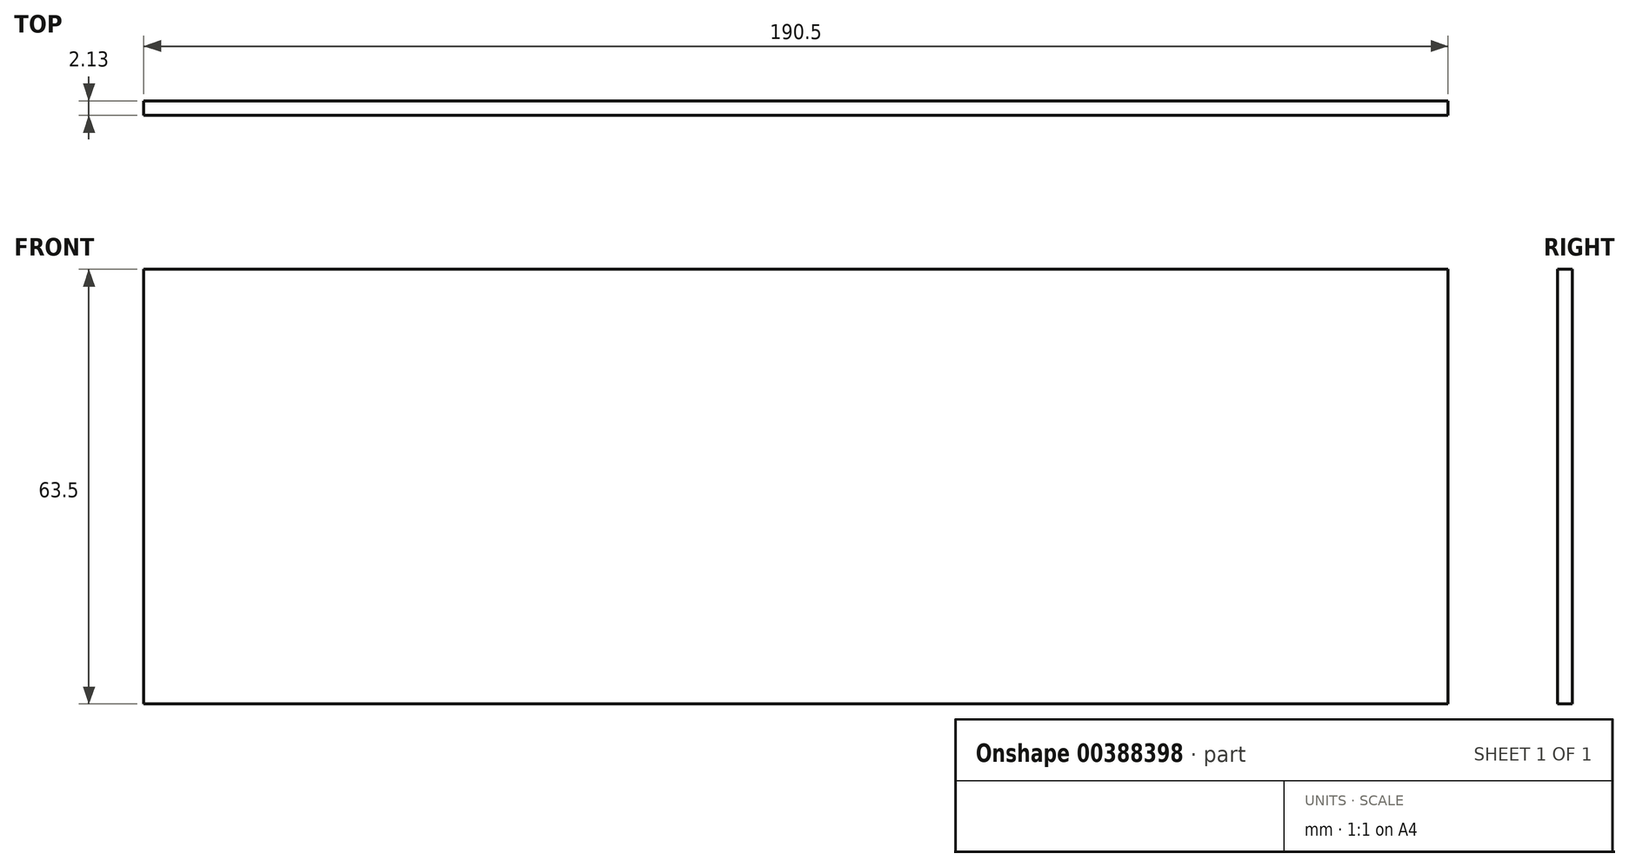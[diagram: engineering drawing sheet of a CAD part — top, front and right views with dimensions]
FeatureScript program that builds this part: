
annotation { "Feature Type Name" : "Feature", "Feature Type Description" : "" }
export const myFeature = defineFeature(function(context is Context, id is Id, definition is map)
    precondition{}
    {
        {
            var Q0;
            Q0=qCreatedBy(makeId("Front.planeOp"),FACE);
            var sketch = newSketch(context, id + "F0", { "sketchPlane" : qUnion([Q0])});
            skLineSegment(sketch, "E0.bottom", {"start": v(0, 0) * mm, "end": v(190.5, 0) * mm});
            skLineSegment(sketch, "E0.top", {"start": v(0, -63.5) * mm, "end": v(190.5, -63.5) * mm});
            skLineSegment(sketch, "E0.left", {"start": v(0, 0) * mm, "end": v(0, -63.5) * mm});
            skLineSegment(sketch, "E0.right", {"start": v(190.5, 0) * mm, "end": v(190.5, -63.5) * mm});
            skSolve(sketch);
        }
        {
            var Q0;
            Q0 = qSketchRegion(id + "F0", true);
            extrude(context, id + "F1", {"entities" : qUnion([Q0]), "depth" : 2.13 * mm});
        }
    });
